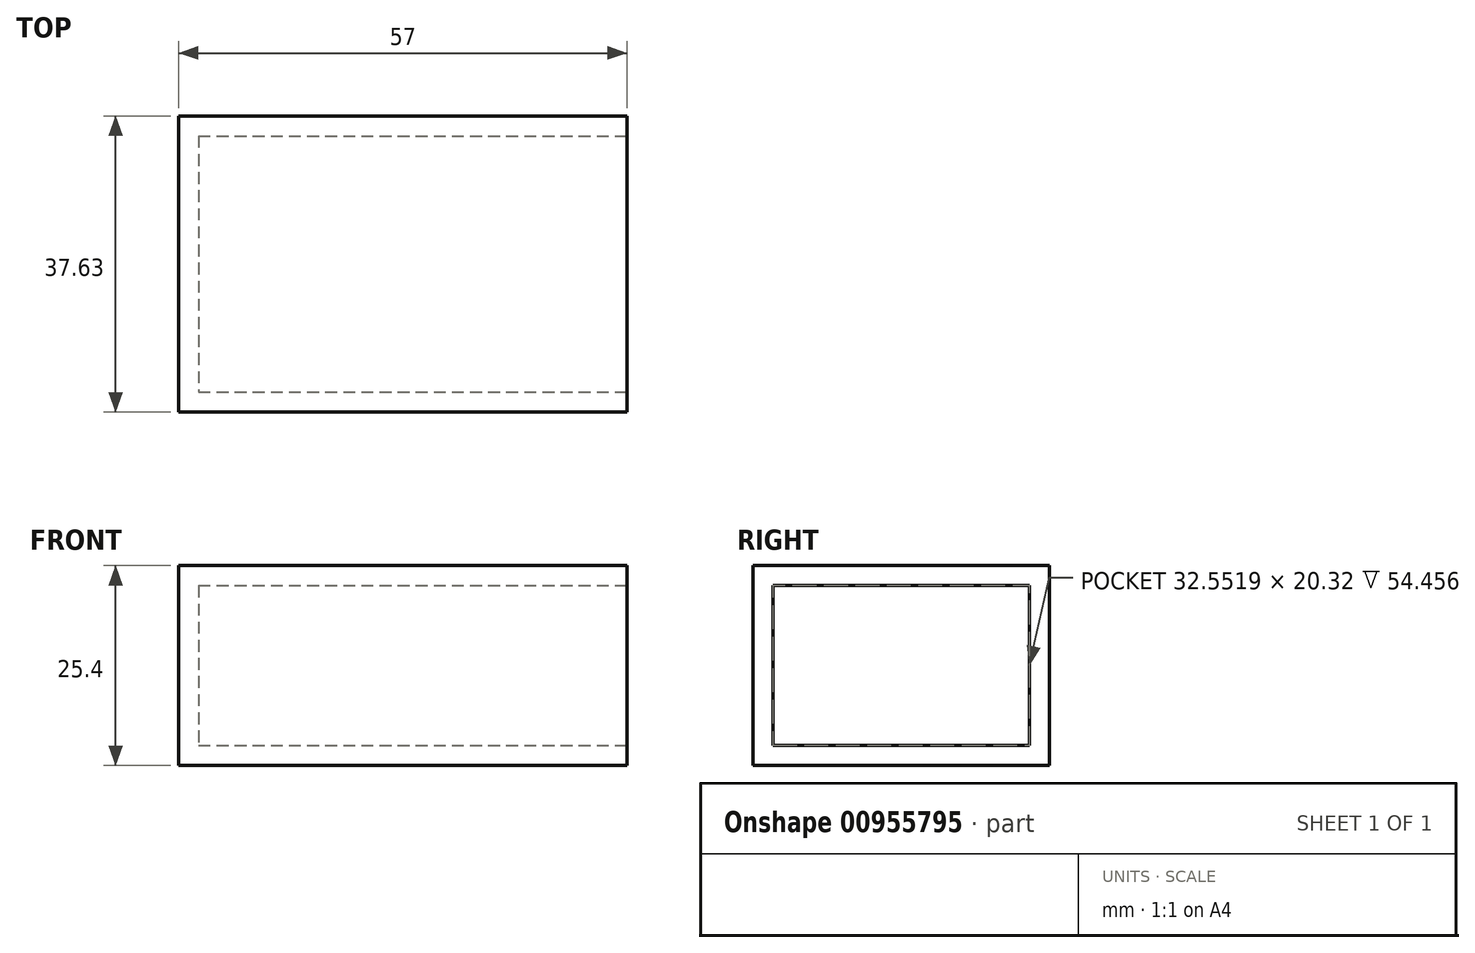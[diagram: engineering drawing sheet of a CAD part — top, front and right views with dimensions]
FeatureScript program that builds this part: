
annotation { "Feature Type Name" : "Feature", "Feature Type Description" : "" }
export const myFeature = defineFeature(function(context is Context, id is Id, definition is map)
    precondition{}
    {
        {
            var Q0;
            Q0=qCreatedBy(makeId("Top.planeOp"),FACE);
            var sketch = newSketch(context, id + "F0", { "sketchPlane" : qUnion([Q0])});
            skLineSegment(sketch, "E0.bottom", {"start": v(-18.77, 14.6) * mm, "end": v(38.23, 14.6) * mm});
            skLineSegment(sketch, "E0.top", {"start": v(-18.77, -23.03) * mm, "end": v(38.23, -23.03) * mm});
            skLineSegment(sketch, "E0.left", {"start": v(-18.77, 14.6) * mm, "end": v(-18.77, -23.03) * mm});
            skLineSegment(sketch, "E0.right", {"start": v(38.23, 14.6) * mm, "end": v(38.23, -23.03) * mm});
            skSolve(sketch);
        }
        {
            var Q0;
            Q0 = qSketchRegion(id + "F0", true);
            extrude(context, id + "F1", {"entities" : qUnion([Q0]), "depth" : 25.4 * mm, "offsetDistance" : 25.4 * mm});
        }
        {
            var Q0;
            Q0=makeQuery(id+"F1.opExtrude","SWEPT_FACE",FACE,{"disambiguationData":[OSD([sQuery(id+"F0.wireOp",EDGE,"E0.right")])]});
            shell(context, id + "F2", {"entities" : qUnion([Q0]), "thickness" : 2.54 * mm});
        }
    });
